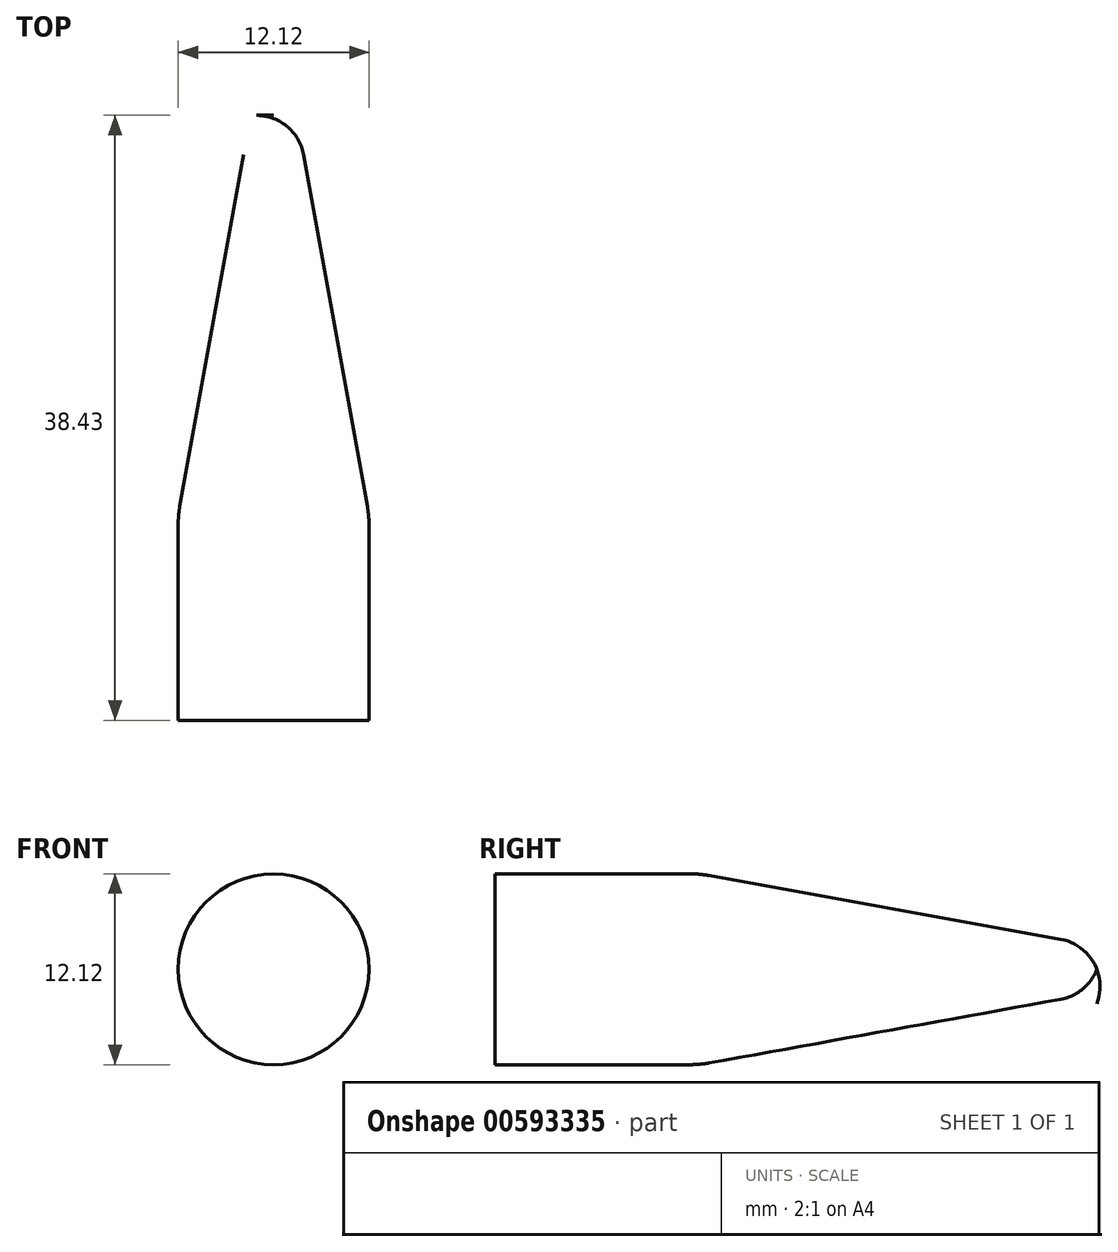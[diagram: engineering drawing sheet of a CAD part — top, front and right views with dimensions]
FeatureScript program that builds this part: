
annotation { "Feature Type Name" : "Feature", "Feature Type Description" : "" }
export const myFeature = defineFeature(function(context is Context, id is Id, definition is map)
    precondition{}
    {
        {
            var Q0;
            Q0=qCreatedBy(makeId("Right.planeOp"),FACE);
            var sketch = newSketch(context, id + "F0", { "sketchPlane" : qUnion([Q0])});
            skLineSegment(sketch, "E0", {"start": v(34.54, 55.63) * mm, "end": v(34.54, 55.63) * mm});
            skPoint(sketch, "E1.orphan", {"position": v(2.16, 0) * mm});
            skPoint(sketch, "E2.end.orphan", {"position": v(2.16, 5.1) * mm});
            skPoint(sketch, "E2.start.orphan", {"position": v(0, 5.1) * mm});
            skPoint(sketch, "E3.orphan", {"position": v(75.43, 0) * mm});
            skPoint(sketch, "E4.end.orphan", {"position": v(76.35, 0) * mm});
            skLineSegment(sketch, "E5", {"start": v(0, 22.27) * mm, "end": v(100.2, 22.27) * mm, "construction": true});
            skPoint(sketch, "E6.start.orphan", {"position": v(87.18, 0) * mm});
            skLineSegment(sketch, "E7", {"start": v(99.63, 6.06) * mm, "end": v(87.18, 6.06) * mm});
            skPoint(sketch, "E8.visualSharp", {"position": v(6.67, 9.78) * mm});
            skPoint(sketch, "E9.end.orphan", {"position": v(87.18, 6.49) * mm});
            skPoint(sketch, "E10.trimOffspring.end.orphan", {"position": v(76.35, 10.21) * mm});
            skPoint(sketch, "E11.start.orphan", {"position": v(76.35, 9.78) * mm});
            skPoint(sketch, "E12.end.orphan", {"position": v(6.67, 10.21) * mm});
            skPoint(sketch, "E13.orphan", {"position": v(0, 10.21) * mm});
            skPoint(sketch, "E14.start.orphan", {"position": v(0, 4.02) * mm});
            skPoint(sketch, "E15.end.orphan", {"position": v(4.41, 4.02) * mm});
            skPoint(sketch, "E15.start.orphan", {"position": v(4.41, 1.46) * mm});
            skPoint(sketch, "E16.start.orphan", {"position": v(0, 0) * mm});
            skLineSegment(sketch, "E17", {"start": v(87.18, 0) * mm, "end": v(125.4, 0) * mm, "construction": true});
            skLineSegment(sketch, "E18", {"start": v(100.76, 5.96) * mm, "end": v(123.1, 1.9) * mm});
            skArc(sketch, "E19", {"start": v(125.4, 0) * mm, "mid": v(124.5, 1.26) * mm, "end": v(123.1, 1.9) * mm});
            skPoint(sketch, "E20.start.orphan", {"position": v(100.2, 6.49) * mm});
            skPoint(sketch, "E21.visualSharp", {"position": v(100.2, 6.06) * mm});
            skArc(sketch, "E21.filletArc", {"start": v(100.76, 5.96) * mm, "mid": v(100.2, 6.03) * mm, "end": v(99.63, 6.06) * mm});
            skLineSegment(sketch, "E22", {"start": v(87.18, 6.06) * mm, "end": v(87.18, 0) * mm});
            skLineSegment(sketch, "E23", {"start": v(87.18, 0) * mm, "end": v(125.4, 0) * mm});
            skSolve(sketch);
        }
        {
            var Q0;
            Q0=makeQuery(id+"F0.imprint","IMPRINT",FACE,{"disambiguationData":[TD([[makeQuery(id+"F0.imprint","IMPRINT",EDGE,{"derivedFrom":sQuery(id+"F0.wireOp",EDGE,"E7")}),1.0]])]});
            var Q1;
            Q1=sQuery(id+"F0.wireOp",EDGE,"E17");
            revolve(context, id + "F1", {"entities" : qUnion([Q0]), "axis" : qUnion([Q1]), "revolveType" : RevolveType.FULL});
        }
    });
